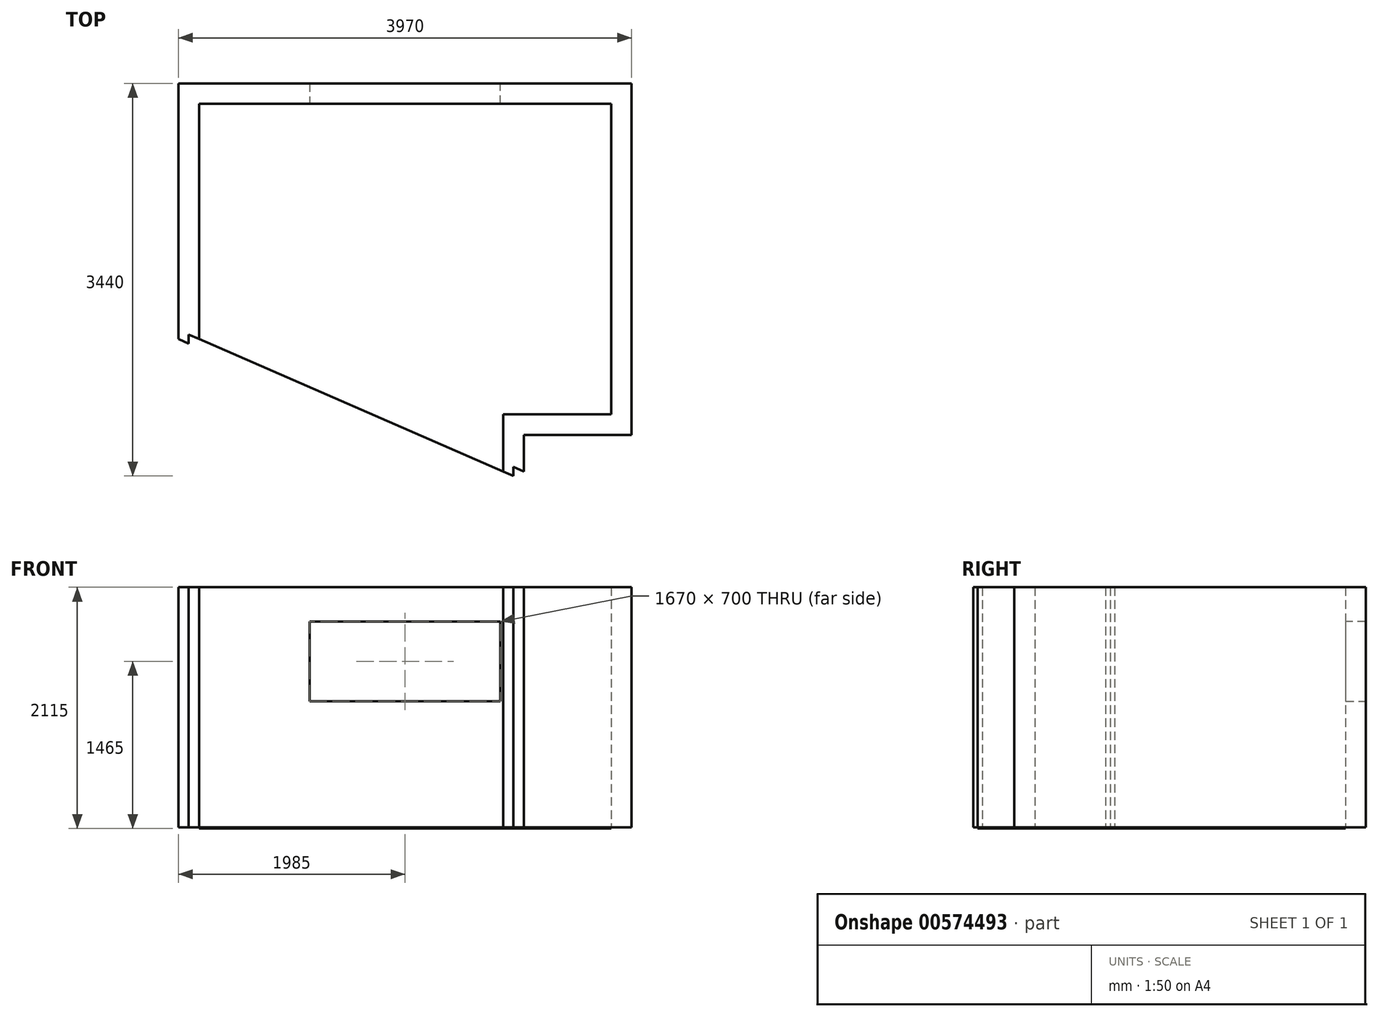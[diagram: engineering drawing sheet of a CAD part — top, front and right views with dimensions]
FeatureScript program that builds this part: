
annotation { "Feature Type Name" : "Feature", "Feature Type Description" : "" }
export const myFeature = defineFeature(function(context is Context, id is Id, definition is map)
    precondition{}
    {
        {
            var Q0;
            Q0=qCreatedBy(makeId("Top.planeOp"),FACE);
            var sketch = newSketch(context, id + "F0", { "sketchPlane" : qUnion([Q0])});
            skLineSegment(sketch, "E0", {"start": v(0, 0) * mm, "end": v(945, 0) * mm});
            skLineSegment(sketch, "E1", {"start": v(945, 0) * mm, "end": v(945, 2720) * mm});
            skLineSegment(sketch, "E2", {"start": v(945, 2720) * mm, "end": v(-2665, 2720) * mm});
            skLineSegment(sketch, "E3", {"start": v(-2665, 2720) * mm, "end": v(-2665, 660) * mm});
            skLineSegment(sketch, "E4", {"start": v(0, 0) * mm, "end": v(0, -500) * mm});
            skLineSegment(sketch, "E5.0", {"start": v(-2845, 2900) * mm, "end": v(-2845, 660) * mm});
            skLineSegment(sketch, "E5.1", {"start": v(180, -180) * mm, "end": v(180, -500) * mm});
            skLineSegment(sketch, "E5.2", {"start": v(180, -180) * mm, "end": v(1125, -180) * mm});
            skLineSegment(sketch, "E5.3", {"start": v(1125, -180) * mm, "end": v(1125, 2900) * mm});
            skLineSegment(sketch, "E5.4", {"start": v(1125, 2900) * mm, "end": v(-2845, 2900) * mm});
            skLineSegment(sketch, "E6", {"start": v(-2845, 660) * mm, "end": v(-2755, 620) * mm});
            skLineSegment(sketch, "E7", {"start": v(-2755, 620) * mm, "end": v(-2755, 700) * mm});
            skLineSegment(sketch, "E8", {"start": v(-2755, 700) * mm, "end": v(-2665, 660) * mm});
            skLineSegment(sketch, "E9", {"start": v(0, -500) * mm, "end": v(90, -540) * mm});
            skLineSegment(sketch, "E10", {"start": v(90, -540) * mm, "end": v(90, -460) * mm});
            skLineSegment(sketch, "E11", {"start": v(90, -460) * mm, "end": v(180, -500) * mm});
            skSolve(sketch);
        }
        {
            var Q0;
            Q0 = qSketchRegion(id + "F0", true);
            extrude(context, id + "F1", {"entities" : qUnion([Q0]), "depth" : (905 + 200) * mm, "offsetDistance" : 25 * mm});
        }
        {
            var Q0;
            Q0=makeQuery(id+"F1.opExtrude","CAP_FACE",FACE,{"disambiguationData":[OSD([sQuery(id+"F0.wireOp",EDGE,"E0"),sQuery(id+"F0.wireOp",EDGE,"E1"),sQuery(id+"F0.wireOp",EDGE,"E2"),sQuery(id+"F0.wireOp",EDGE,"E3"),sQuery(id+"F0.wireOp",EDGE,"E4"),sQuery(id+"F0.wireOp",EDGE,"E5.0"),sQuery(id+"F0.wireOp",EDGE,"E5.1"),sQuery(id+"F0.wireOp",EDGE,"E5.2"),sQuery(id+"F0.wireOp",EDGE,"E5.3"),sQuery(id+"F0.wireOp",EDGE,"E5.4"),sQuery(id+"F0.wireOp",EDGE,"E6"),sQuery(id+"F0.wireOp",EDGE,"E7"),sQuery(id+"F0.wireOp",EDGE,"E8"),sQuery(id+"F0.wireOp",EDGE,"E9"),sQuery(id+"F0.wireOp",EDGE,"E10"),sQuery(id+"F0.wireOp",EDGE,"E11")])],"isStart":false});
            var sketch = newSketch(context, id + "F2", { "sketchPlane" : qUnion([Q0])});
            skLineSegment(sketch, "E12", {"start": v(-1695, 2720) * mm, "end": v(-2665, 2720) * mm});
            skLineSegment(sketch, "E13", {"start": v(-2665, 2720) * mm, "end": v(-2665, 660) * mm});
            skLineSegment(sketch, "E14", {"start": v(-2665, 660) * mm, "end": v(-2755, 700) * mm});
            skLineSegment(sketch, "E15", {"start": v(-2755, 700) * mm, "end": v(-2755, 620) * mm});
            skLineSegment(sketch, "E16", {"start": v(-2755, 620) * mm, "end": v(-2845, 660) * mm});
            skLineSegment(sketch, "E17", {"start": v(-2845, 660) * mm, "end": v(-2845, 2900) * mm});
            skLineSegment(sketch, "E18", {"start": v(-2845, 2900) * mm, "end": v(-1695, 2900) * mm});
            skLineSegment(sketch, "E19", {"start": v(-1695, 2900) * mm, "end": v(-1695, 2720) * mm});
            skLineSegment(sketch, "E20", {"start": v(0, -500) * mm, "end": v(0, 0) * mm});
            skLineSegment(sketch, "E21", {"start": v(0, 0) * mm, "end": v(945, 0) * mm});
            skLineSegment(sketch, "E22", {"start": v(945, 0) * mm, "end": v(945, 2720) * mm});
            skLineSegment(sketch, "E23", {"start": v(945, 2720) * mm, "end": v(-25, 2720) * mm});
            skLineSegment(sketch, "E24", {"start": v(-25, 2720) * mm, "end": v(-25, 2900) * mm});
            skLineSegment(sketch, "E25", {"start": v(-25, 2900) * mm, "end": v(1125, 2900) * mm});
            skLineSegment(sketch, "E26", {"start": v(1125, 2900) * mm, "end": v(1125, -180) * mm});
            skLineSegment(sketch, "E27", {"start": v(1125, -180) * mm, "end": v(180, -180) * mm});
            skLineSegment(sketch, "E28", {"start": v(180, -180) * mm, "end": v(180, -500) * mm});
            skLineSegment(sketch, "E29", {"start": v(180, -500) * mm, "end": v(90, -460) * mm});
            skLineSegment(sketch, "E30", {"start": v(90, -460) * mm, "end": v(90, -540) * mm});
            skLineSegment(sketch, "E31", {"start": v(90, -540) * mm, "end": v(0, -500) * mm});
            skSolve(sketch);
        }
        {
            var Q0;
            Q0 = qSketchRegion(id + "F2", true);
            extrude(context, id + "F3", {"entities" : qUnion([Q0]), "operationType" : NewBodyOperationType.ADD, "depth" : 700 * mm, "offsetDistance" : 25 * mm});
        }
        {
            var Q0;
            Q0=makeQuery(id+"F3.opExtrude","CAP_FACE",FACE,{"disambiguationData":[OSD([sQuery(id+"F2.wireOp",EDGE,"E12"),sQuery(id+"F2.wireOp",EDGE,"E13"),sQuery(id+"F2.wireOp",EDGE,"E14"),sQuery(id+"F2.wireOp",EDGE,"E15"),sQuery(id+"F2.wireOp",EDGE,"E16"),sQuery(id+"F2.wireOp",EDGE,"E17"),sQuery(id+"F2.wireOp",EDGE,"E18"),sQuery(id+"F2.wireOp",EDGE,"E19")])],"isStart":false});
            var sketch = newSketch(context, id + "F4", { "sketchPlane" : qUnion([Q0])});
            skLineSegment(sketch, "E32", {"start": v(-2845, 660) * mm, "end": v(-2845, 2900) * mm});
            skLineSegment(sketch, "E33", {"start": v(-2845, 2900) * mm, "end": v(1125, 2900) * mm});
            skLineSegment(sketch, "E34", {"start": v(1125, 2900) * mm, "end": v(1125, -180) * mm});
            skLineSegment(sketch, "E35", {"start": v(1125, -180) * mm, "end": v(180, -180) * mm});
            skLineSegment(sketch, "E36", {"start": v(180, -180) * mm, "end": v(180, -500) * mm});
            skLineSegment(sketch, "E37", {"start": v(180, -500) * mm, "end": v(90, -460) * mm});
            skLineSegment(sketch, "E38", {"start": v(90, -460) * mm, "end": v(90, -540) * mm});
            skLineSegment(sketch, "E39", {"start": v(90, -540) * mm, "end": v(0, -500) * mm});
            skLineSegment(sketch, "E40", {"start": v(0, -500) * mm, "end": v(0, 0) * mm});
            skLineSegment(sketch, "E41", {"start": v(0, 0) * mm, "end": v(945, 0) * mm});
            skLineSegment(sketch, "E42", {"start": v(945, 0) * mm, "end": v(945, 2720) * mm});
            skLineSegment(sketch, "E43", {"start": v(945, 2720) * mm, "end": v(-2665, 2720) * mm});
            skLineSegment(sketch, "E44", {"start": v(-2665, 2720) * mm, "end": v(-2665, 660) * mm});
            skLineSegment(sketch, "E45", {"start": v(-2665, 660) * mm, "end": v(-2755, 700) * mm});
            skLineSegment(sketch, "E46", {"start": v(-2755, 700) * mm, "end": v(-2755, 620) * mm});
            skLineSegment(sketch, "E47", {"start": v(-2755, 620) * mm, "end": v(-2845, 660) * mm});
            skSolve(sketch);
        }
        {
            var Q0;
            Q0 = qSketchRegion(id + "F4", true);
            extrude(context, id + "F5", {"entities" : qUnion([Q0]), "operationType" : NewBodyOperationType.ADD, "depth" : 300 * mm, "offsetDistance" : 25 * mm});
        }
        {
            var Q0;
            Q0=qCreatedBy(makeId("Top.planeOp"),FACE);
            var sketch = newSketch(context, id + "F6", { "sketchPlane" : qUnion([Q0])});
            skLineSegment(sketch, "E48", {"start": v(0, 0) * mm, "end": v(945, 0) * mm});
            skLineSegment(sketch, "E49", {"start": v(945, 0) * mm, "end": v(945, 2720) * mm});
            skLineSegment(sketch, "E50", {"start": v(945, 2720) * mm, "end": v(-2665, 2720) * mm});
            skLineSegment(sketch, "E51", {"start": v(-2665, 2720) * mm, "end": v(-2665, 660) * mm});
            skLineSegment(sketch, "E52", {"start": v(0, 0) * mm, "end": v(0, -500) * mm});
            skLineSegment(sketch, "E53", {"start": v(0, -500) * mm, "end": v(-2665, 660) * mm});
            skSolve(sketch);
        }
        {
            var Q0;
            Q0 = qSketchRegion(id + "F6", true);
            extrude(context, id + "F7", {"entities" : qUnion([Q0]), "oppositeDirection" : true, "depth" : 10 * mm, "offsetDistance" : 25 * mm});
        }
    });
